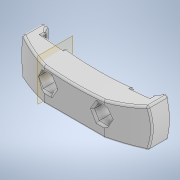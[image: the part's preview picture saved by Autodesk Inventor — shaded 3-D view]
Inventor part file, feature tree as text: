
AUTODESK INVENTOR PART (.ipt)
format: ipt  version: 2020.3 (Build 243373000, 373)  size: 458,240 bytes
history: native  units: mm
features: extrude x4, sketch x4, fillet x3, plane x1, mirror x1
ambient origin geometry x8: Origin, YZ Plane, XZ Plane, XY Plane, X Axis, Y Axis, Z Axis, Center Point
bodies: Volumenkörper1 (feature_tree)
feature tree (13):
  extrude  "Extrusion1"  Depth=20.0mm
  plane  "Arbeitsebene1"
  extrude  "Extrusion2"  Depth=10.0mm TaperAngle=0.0deg
  fillet  "Rundung1"  Radius=5.5mm
  extrude  "Extrusion3"  Depth=29.0mm
  extrude  "Extrusion4"  Depth=1.0mm
  mirror  "Spiegeln1"
  fillet  "Rundung3"  Radius=7.0mm
  fillet  "Rundung4"  Radius=1.0mm
  sketch  "Skizze1"  dims[d0=68.0mm d1=20.0mm]
  sketch  "Skizze2"  dims[d2=10.0mm d3=16.5mm d4=0.0mm d5=5.5mm]
  sketch  "Skizze3"  dims[d6=5.5mm d7=29.0mm]
  sketch  "Skizze4"  dims[d8=14.5mm d9=8.5mm d10=68.0mm d11=20.0mm d12=10.0mm d13=5.5mm d14=5.5mm d15=29.0mm d16=14.5mm d17=8.5mm d18=7.0mm d19=0.0mm d20=1.0mm d21=75.0mm d22=4.0mm d25=4.0mm d26=3.0mm d27=3.0mm d28=10.0mm d29=0.0mm d30=0.0mm d31=150.0mm d33=-18.0mm d34=40.0mm d35=10.0mm d36=0.0mm d37=1.0mm d38=1.0mm]
